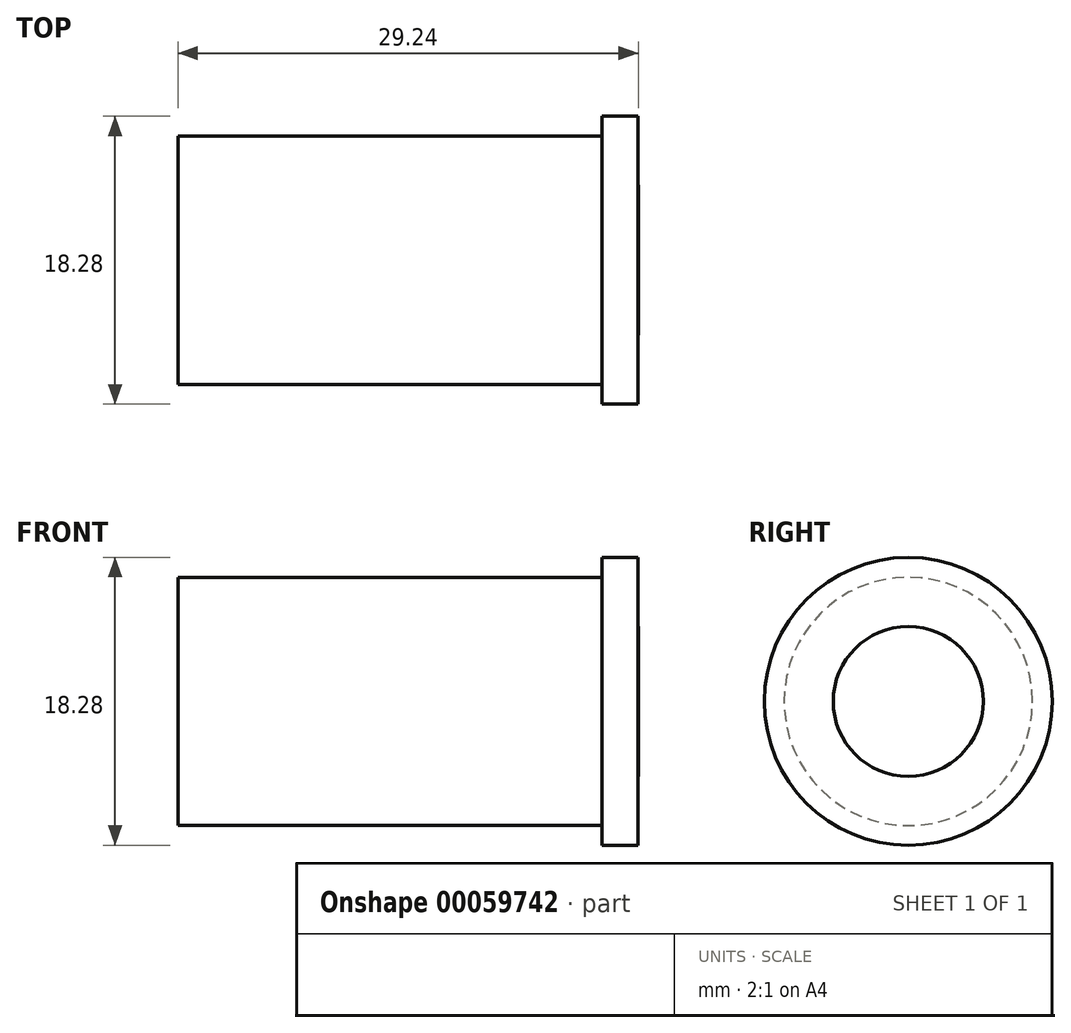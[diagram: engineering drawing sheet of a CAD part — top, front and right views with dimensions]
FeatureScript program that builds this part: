
annotation { "Feature Type Name" : "Feature", "Feature Type Description" : "" }
export const myFeature = defineFeature(function(context is Context, id is Id, definition is map)
    precondition{}
    {
        {
            var Q0;
            Q0=qCreatedBy(makeId("Right.planeOp"),FACE);
            var sketch = newSketch(context, id + "F0", { "sketchPlane" : qUnion([Q0])});
            skCircle(sketch, "E0", {"center": v(0, 0) * mm, "radius": 7.89 * mm});
            skCircle(sketch, "E1", {"center": v(0, 0) * mm, "radius": 9.14 * mm});
            skSolve(sketch);
        }
        {
            var Q0;
            Q0=makeQuery(id+"F0.imprint","IMPRINT",FACE,{"disambiguationData":[TD([[makeQuery(id+"F0.imprint","IMPRINT",EDGE,{"derivedFrom":sQuery(id+"F0.wireOp",EDGE,"E0")}),1.0]])]});
            extrude(context, id + "F1", {"entities" : qUnion([Q0]), "oppositeDirection" : true, "depth" : 26.92 * mm});
        }
        {
            var Q0;
            Q0=makeQuery(id+"F0.imprint","IMPRINT",FACE,{"disambiguationData":[TD([[makeQuery(id+"F0.imprint","IMPRINT",EDGE,{"derivedFrom":sQuery(id+"F0.wireOp",EDGE,"E0")}),-1.0]])]});
            var Q1;
            Q1=makeQuery(id+"F0.imprint","IMPRINT",FACE,{"disambiguationData":[TD([[makeQuery(id+"F0.imprint","IMPRINT",EDGE,{"derivedFrom":sQuery(id+"F0.wireOp",EDGE,"E0")}),1.0]])]});
            extrude(context, id + "F2", {"entities" : qUnion([Q0, Q1]), "operationType" : NewBodyOperationType.ADD, "depth" : 2.3 * mm});
        }
        {
            var Q0;
            Q0=makeQuery(id+"F2.opExtrude","CAP_FACE",FACE,{"disambiguationData":[OSD([sQuery(id+"F0.wireOp",EDGE,"E1")])],"isStart":false});
            var sketch = newSketch(context, id + "F3", { "sketchPlane" : qUnion([Q0])});
            skCircle(sketch, "E2", {"center": v(0, 0) * mm, "radius": 4.76 * mm});
            skSolve(sketch);
        }
        {
            var Q0;
            Q0=makeQuery(id+"F3.imprint","IMPRINT",FACE,{"disambiguationData":[TD([[makeQuery(id+"F3.imprint","IMPRINT",EDGE,{"derivedFrom":sQuery(id+"F3.wireOp",EDGE,"E2")}),1.0]])]});
            extrude(context, id + "F4", {"entities" : qUnion([Q0]), "operationType" : NewBodyOperationType.ADD, "depth" : 7 / 203.2 * mm});
        }
    });
